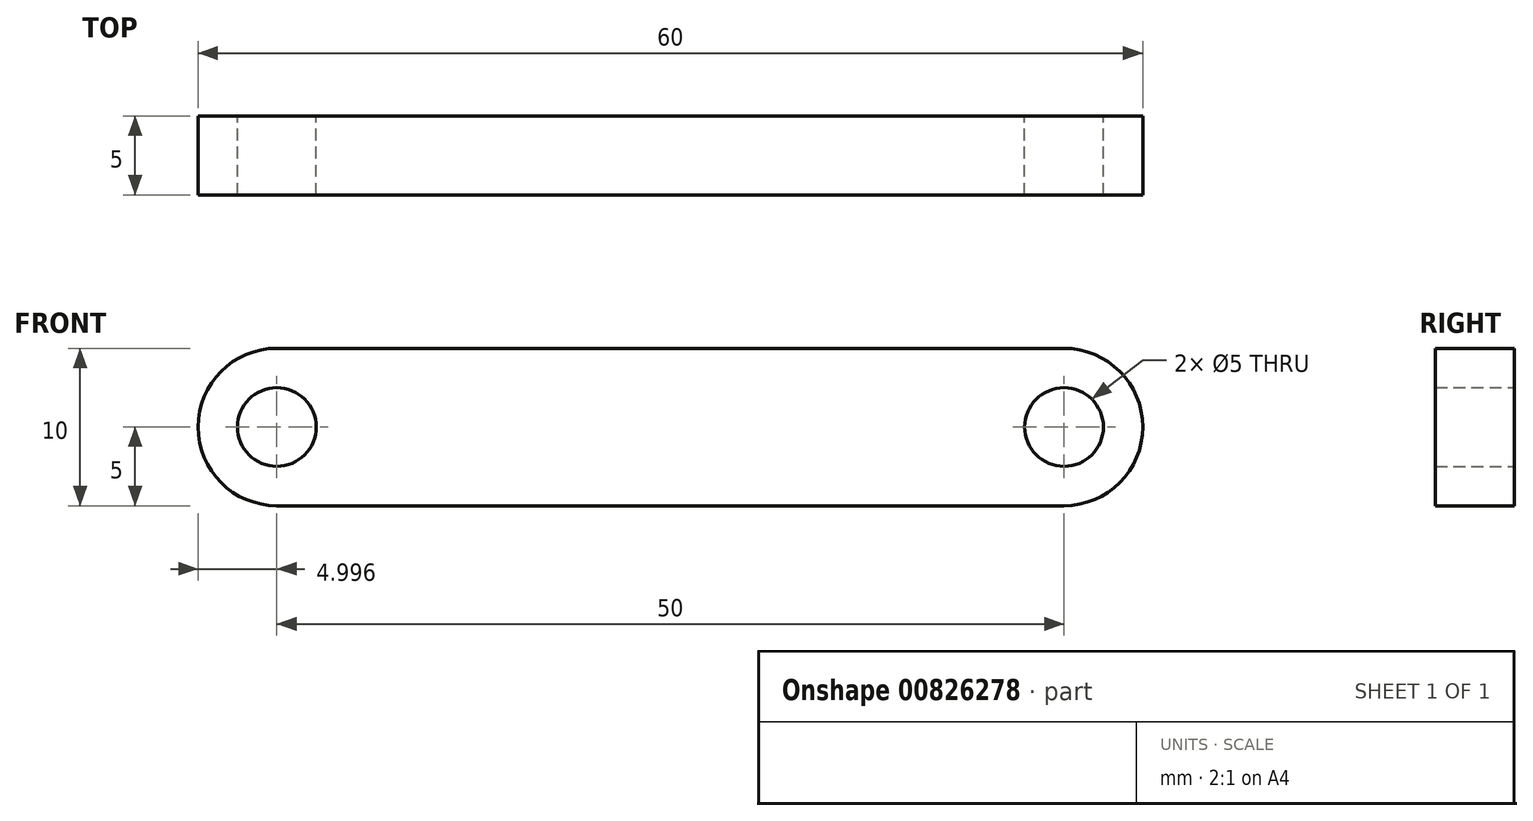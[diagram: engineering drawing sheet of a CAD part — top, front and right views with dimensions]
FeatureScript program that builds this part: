
annotation { "Feature Type Name" : "Feature", "Feature Type Description" : "" }
export const myFeature = defineFeature(function(context is Context, id is Id, definition is map)
    precondition{}
    {
        {
            var Q0;
            Q0=qCreatedBy(makeId("Front.planeOp"),FACE);
            var sketch = newSketch(context, id + "F0", { "sketchPlane" : qUnion([Q0])});
            skArc(sketch, "E0", {"start": v(-13.14, 20.02) * mm, "mid": v(-18.14, 15.02) * mm, "end": v(-13.14, 10.02) * mm});
            skArc(sketch, "E1", {"start": v(36.86, 10.02) * mm, "mid": v(41.86, 15.02) * mm, "end": v(36.86, 20.02) * mm});
            skLineSegment(sketch, "E2", {"start": v(-13.14, 20.02) * mm, "end": v(36.86, 20.02) * mm});
            skLineSegment(sketch, "E3", {"start": v(-13.14, 10.02) * mm, "end": v(36.86, 10.02) * mm});
            skCircle(sketch, "E4", {"center": v(-13.14, 15.02) * mm, "radius": 2.5 * mm});
            skCircle(sketch, "E5", {"center": v(36.86, 15.02) * mm, "radius": 2.5 * mm});
            skSolve(sketch);
        }
        {
            var Q0;
            Q0 = qSketchRegion(id + "F0", true);
            extrude(context, id + "F1", {"entities" : qUnion([Q0]), "depth" : 5 * mm, "offsetDistance" : 25 * mm});
        }
    });
